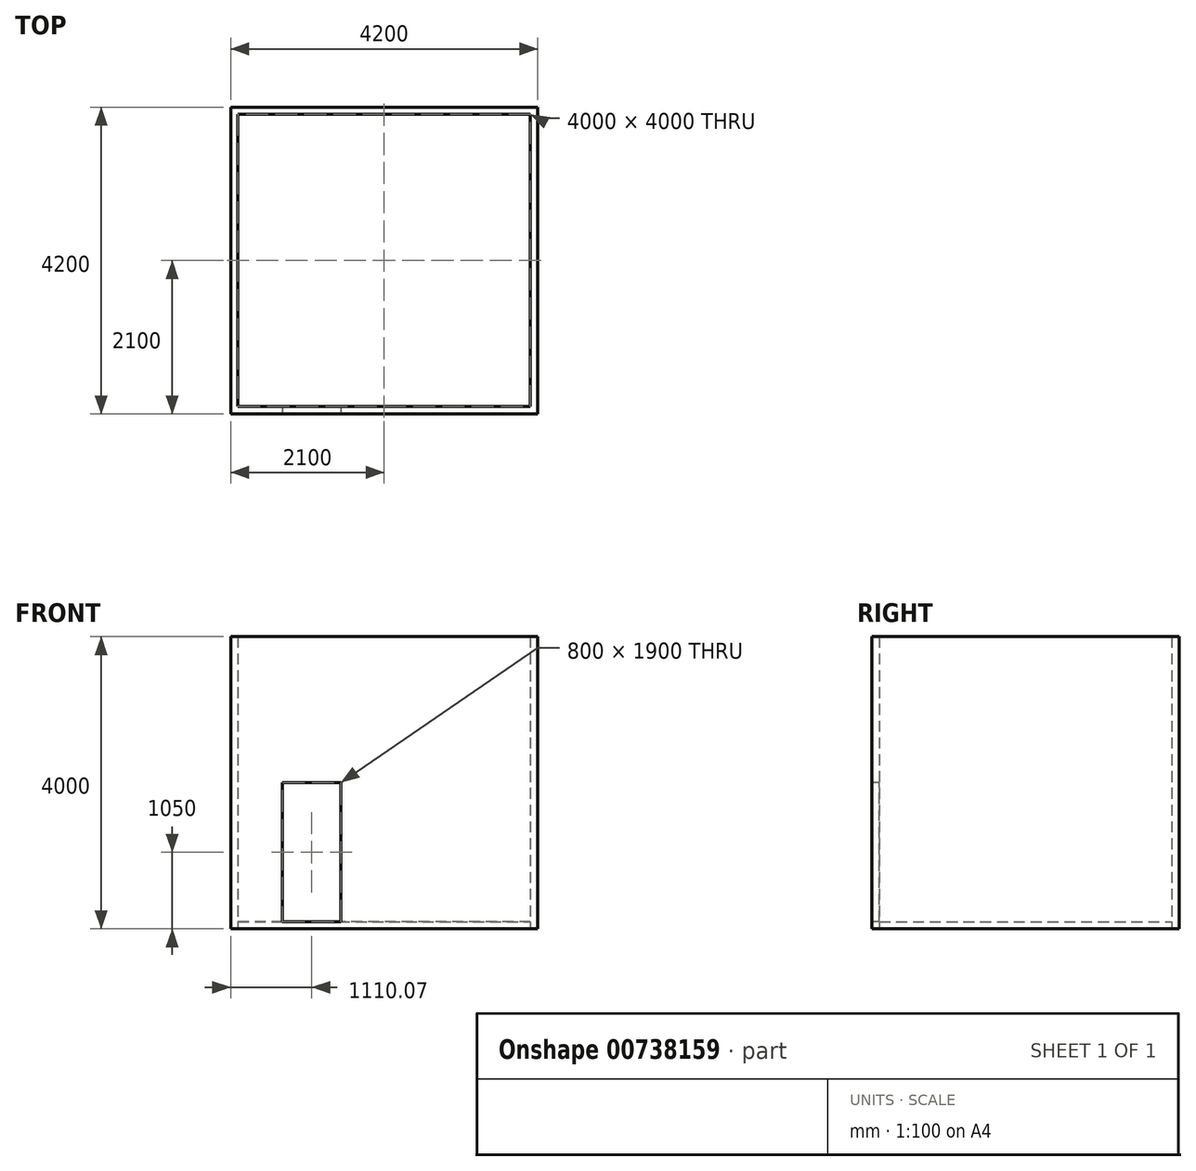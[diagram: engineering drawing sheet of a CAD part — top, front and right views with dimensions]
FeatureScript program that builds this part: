
annotation { "Feature Type Name" : "Feature", "Feature Type Description" : "" }
export const myFeature = defineFeature(function(context is Context, id is Id, definition is map)
    precondition{}
    {
        {
            var Q0;
            Q0=qCreatedBy(makeId("Top.planeOp"),FACE);
            var sketch = newSketch(context, id + "F0", { "sketchPlane" : qUnion([Q0])});
            skLineSegment(sketch, "E0", {"start": v(-5029.27, 4000) * mm, "end": v(-1029.27, 4000) * mm});
            skLineSegment(sketch, "E1", {"start": v(-1029.27, 4000) * mm, "end": v(-1029.27, 0) * mm});
            skLineSegment(sketch, "E2", {"start": v(-1029.27, 0) * mm, "end": v(-5029.27, 0) * mm});
            skLineSegment(sketch, "E3", {"start": v(-5029.27, 0) * mm, "end": v(-5029.27, 4000) * mm});
            skLineSegment(sketch, "E4.0", {"start": v(-5129.27, -100) * mm, "end": v(-5129.27, 4100) * mm});
            skLineSegment(sketch, "E4.1", {"start": v(-929.27, -100) * mm, "end": v(-5129.27, -100) * mm});
            skLineSegment(sketch, "E4.2", {"start": v(-929.27, 4100) * mm, "end": v(-929.27, -100) * mm});
            skLineSegment(sketch, "E4.3", {"start": v(-5129.27, 4100) * mm, "end": v(-929.27, 4100) * mm});
            skSolve(sketch);
        }
        {
            var Q0;
            Q0=makeQuery(id+"F0.imprint","IMPRINT",FACE,{"disambiguationData":[TD([[makeQuery(id+"F0.imprint","IMPRINT",EDGE,{"derivedFrom":sQuery(id+"F0.wireOp",EDGE,"E0")}),1.0]])]});
            var Q1;
            Q1=sQuery(id+"F0.wireOp",EDGE,"E4.3");
            extrude(context, id + "F1", {"entities" : qUnion([Q0]), "surfaceEntities" : qUnion([Q1]), "depth" : 4000 * mm, "offsetDistance" : 25 * mm});
        }
        {
            var Q0;
            Q0=makeQuery(id+"F0.imprint","IMPRINT",FACE,{"disambiguationData":[TD([[makeQuery(id+"F0.imprint","IMPRINT",EDGE,{"derivedFrom":sQuery(id+"F0.wireOp",EDGE,"E0")}),-1.0]])]});
            extrude(context, id + "F2", {"entities" : qUnion([Q0]), "depth" : 100 * mm, "offsetDistance" : 25 * mm});
        }
        {
            var Q0;
            Q0=makeQuery(id+"F1.opExtrude","SWEPT_FACE",FACE,{"disambiguationData":[OSD([sQuery(id+"F0.wireOp",EDGE,"E4.1")])]});
            var sketch = newSketch(context, id + "F3", { "sketchPlane" : qUnion([Q0])});
            skLineSegment(sketch, "E5.0", {"start": v(-3619.2, 100) * mm, "end": v(-3619.2, 2000) * mm});
            skLineSegment(sketch, "E6.0", {"start": v(-4419.2, 100) * mm, "end": v(-4419.2, 2000) * mm});
            skLineSegment(sketch, "E7", {"start": v(-4419.2, 2000) * mm, "end": v(-3619.2, 2000) * mm});
            skPoint(sketch, "E8.end.orphan", {"position": v(-3029.27, 2000) * mm});
            skPoint(sketch, "E9.orphan", {"position": v(-5129.27, 4000) * mm});
            skPoint(sketch, "E10.orphan", {"position": v(-929.27, 0) * mm});
            skPoint(sketch, "E11.end.orphan", {"position": v(-3029.27, 0) * mm});
            skLineSegment(sketch, "E12.0", {"start": v(-4419.2, 100) * mm, "end": v(-3619.2, 100) * mm});
            skSolve(sketch);
        }
        {
            var Q0;
            Q0=makeQuery(id+"F3.imprint","IMPRINT",FACE,{"disambiguationData":[TD([[makeQuery(id+"F3.imprint","IMPRINT",EDGE,{"derivedFrom":sQuery(id+"F3.wireOp",EDGE,"E5.0")}),1.0]])]});
            extrude(context, id + "F4", {"entities" : qUnion([Q0]), "operationType" : NewBodyOperationType.REMOVE, "oppositeDirection" : true, "depth" : 100 * mm, "offsetDistance" : 25 * mm});
        }
    });
